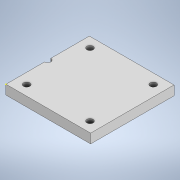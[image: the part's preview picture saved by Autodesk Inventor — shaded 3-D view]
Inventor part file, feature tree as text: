
AUTODESK INVENTOR PART (.ipt)
format: ipt  version: 2022 (Build 260153000, 153)  size: 108,544 bytes
history: native  units: in
note: dims shown in document units (in); Inventor stores cm internally (conversion verified against a paired STEP export)
features: sketch x4, extrude x2, hole x1
ambient origin geometry x8: Origin, YZ Plane, XZ Plane, XY Plane, X Axis, Y Axis, Z Axis, Center Point
bodies: Solid1 (feature_tree)
feature tree (7):
  extrude  "Extrusion1"  Depth=1.0472in
  extrude  "Extrusion2"  Depth=0.0787in
  hole  "Hole1"  [1 undecoded]
  sketch  "Sketch4"  dims[d7=0.0787in d8=0.2362in d9=0.1575in d10=0.0787in d11=90.0deg d12=0.315in d13=0.8108in]
  sketch  "Sketch1"  dims[d0=1.063in d1=1.0472in]
  sketch  "Sketch2"  dims[d2=0.1181in d3=0.0in d4=0.0787in]
  sketch  "Sketch3"  dims[d5=0.0394in d6=0.0in]
note: 1 required parameter value undecoded (feature->parameter linkage not recoverable at this tier; creation-order binding heuristic only, values carry confidence <= 0.55)
